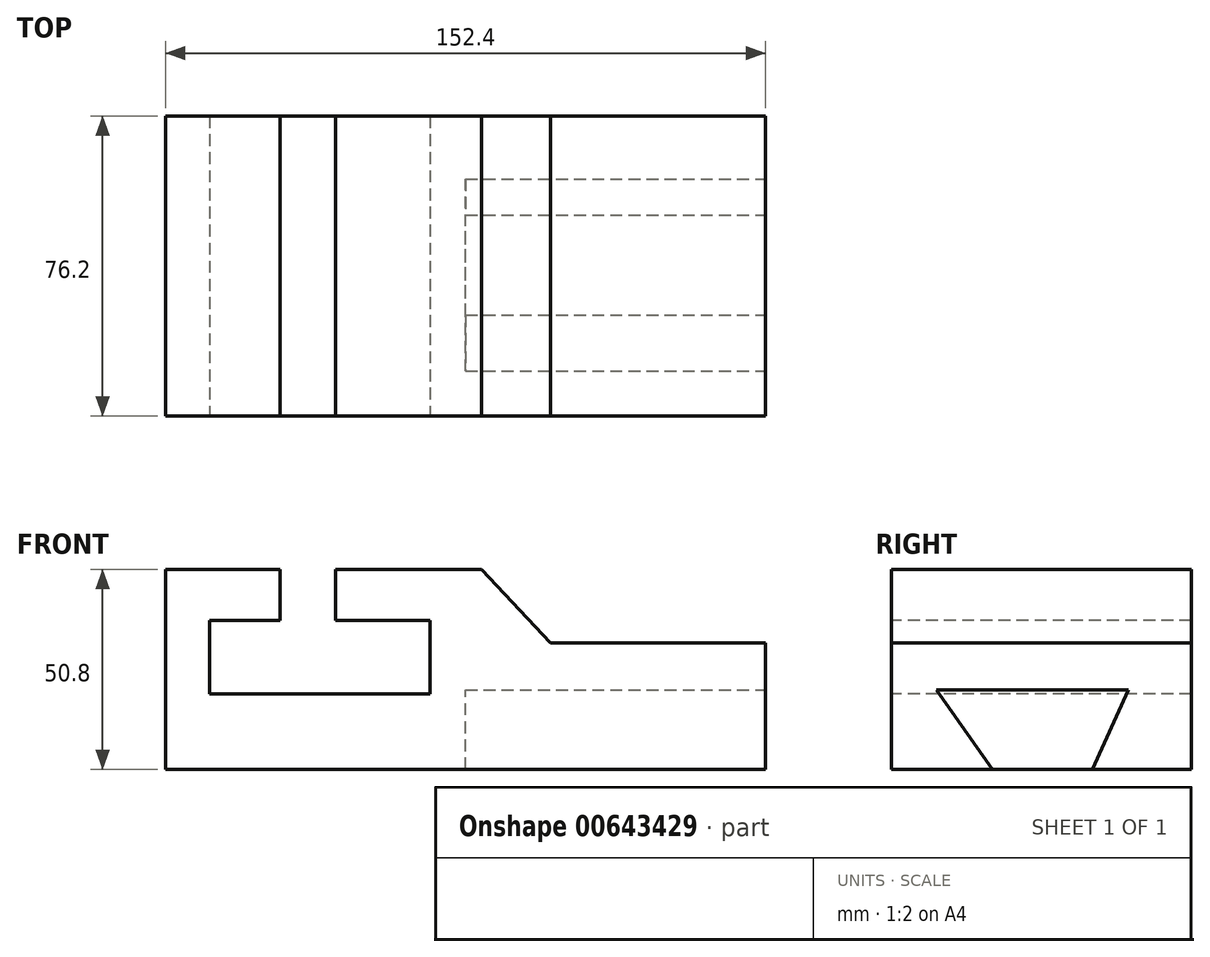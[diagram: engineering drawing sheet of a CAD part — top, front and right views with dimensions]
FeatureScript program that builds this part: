
annotation { "Feature Type Name" : "Feature", "Feature Type Description" : "" }
export const myFeature = defineFeature(function(context is Context, id is Id, definition is map)
    precondition{}
    {
        {
            var Q0;
            Q0=qCreatedBy(makeId("Top.planeOp"),FACE);
            var sketch = newSketch(context, id + "F0", { "sketchPlane" : qUnion([Q0])});
            skLineSegment(sketch, "E0.bottom", {"start": v(138.22, -2.13) * mm, "end": v(290.62, -2.13) * mm});
            skLineSegment(sketch, "E0.top", {"start": v(138.22, 74.07) * mm, "end": v(290.62, 74.07) * mm});
            skLineSegment(sketch, "E0.left", {"start": v(138.22, -2.13) * mm, "end": v(138.22, 74.07) * mm});
            skLineSegment(sketch, "E0.right", {"start": v(290.62, -2.13) * mm, "end": v(290.62, 74.07) * mm});
            skSolve(sketch);
        }
        {
            var Q0;
            Q0=makeQuery(id+"F0.imprint","IMPRINT",FACE,{"disambiguationData":[TD([[makeQuery(id+"F0.imprint","IMPRINT",EDGE,{"derivedFrom":sQuery(id+"F0.wireOp",EDGE,"E0.bottom")}),1.0]])]});
            extrude(context, id + "F1", {"entities" : qUnion([Q0]), "depth" : 50.8 * mm, "offsetDistance" : 25.4 * mm});
        }
        {
            var Q0;
            Q0=makeQuery(id+"F1.opExtrude","SWEPT_FACE",FACE,{"disambiguationData":[OSD([sQuery(id+"F0.wireOp",EDGE,"E0.bottom")])]});
            var sketch = newSketch(context, id + "F2", { "sketchPlane" : qUnion([Q0])});
            skLineSegment(sketch, "E1", {"start": v(138.22, 50.8) * mm, "end": v(167.32, 50.8) * mm});
            skLineSegment(sketch, "E2", {"start": v(167.32, 50.8) * mm, "end": v(167.32, 37.91) * mm});
            skLineSegment(sketch, "E3", {"start": v(167.32, 37.91) * mm, "end": v(149.44, 37.91) * mm});
            skLineSegment(sketch, "E4", {"start": v(149.44, 37.91) * mm, "end": v(149.44, 19.17) * mm});
            skLineSegment(sketch, "E5", {"start": v(149.44, 19.17) * mm, "end": v(205.37, 19.17) * mm});
            skLineSegment(sketch, "E6", {"start": v(205.37, 19.17) * mm, "end": v(205.37, 37.91) * mm});
            skLineSegment(sketch, "E7", {"start": v(205.37, 37.91) * mm, "end": v(181.45, 37.91) * mm});
            skLineSegment(sketch, "E8", {"start": v(181.45, 37.91) * mm, "end": v(181.45, 50.8) * mm});
            skLineSegment(sketch, "E9", {"start": v(181.45, 50.8) * mm, "end": v(167.32, 50.8) * mm});
            skSolve(sketch);
        }
        {
            var Q0;
            Q0=makeQuery(id+"F2.imprint","IMPRINT",FACE,{"disambiguationData":[TD([[makeQuery(id+"F2.imprint","IMPRINT",EDGE,{"derivedFrom":sQuery(id+"F2.wireOp",EDGE,"E2")}),1.0]])]});
            extrude(context, id + "F3", {"entities" : qUnion([Q0]), "operationType" : NewBodyOperationType.REMOVE, "oppositeDirection" : true, "depth" : 76.2 * mm, "offsetDistance" : 25.4 * mm});
        }
        {
            var Q0;
            Q0=makeQuery(id+"F1.opExtrude","SWEPT_FACE",FACE,{"disambiguationData":[OSD([sQuery(id+"F0.wireOp",EDGE,"E0.bottom")])]});
            var sketch = newSketch(context, id + "F4", { "sketchPlane" : qUnion([Q0])});
            skLineSegment(sketch, "E10", {"start": v(218.44, 50.8) * mm, "end": v(236.03, 32.16) * mm});
            skPoint(sketch, "E10.endSnap0", {"position": v(236.03, 50.8) * mm});
            skLineSegment(sketch, "E11", {"start": v(236.03, 32.16) * mm, "end": v(290.62, 32.16) * mm});
            skLineSegment(sketch, "E12", {"start": v(290.62, 32.16) * mm, "end": v(290.62, 50.8) * mm});
            skLineSegment(sketch, "E13", {"start": v(290.62, 50.8) * mm, "end": v(218.44, 50.8) * mm});
            skSolve(sketch);
        }
        {
            var Q0;
            Q0=makeQuery(id+"F4.imprint","IMPRINT",FACE,{"disambiguationData":[TD([[makeQuery(id+"F4.imprint","IMPRINT",EDGE,{"derivedFrom":sQuery(id+"F4.wireOp",EDGE,"E10")}),1.0]])]});
            extrude(context, id + "F5", {"entities" : qUnion([Q0]), "operationType" : NewBodyOperationType.REMOVE, "oppositeDirection" : true, "depth" : 76.2 * mm, "offsetDistance" : 25.4 * mm});
        }
        {
            var Q0;
            Q0=makeQuery(id+"F1.opExtrude","SWEPT_FACE",FACE,{"disambiguationData":[OSD([sQuery(id+"F0.wireOp",EDGE,"E0.right")])]});
            var sketch = newSketch(context, id + "F6", { "sketchPlane" : qUnion([Q0])});
            skLineSegment(sketch, "E14", {"start": v(23.5, 0) * mm, "end": v(9.27, 20.2) * mm});
            skLineSegment(sketch, "E15", {"start": v(9.27, 20.2) * mm, "end": v(58.04, 20.2) * mm});
            skLineSegment(sketch, "E16", {"start": v(58.04, 20.2) * mm, "end": v(48.9, 0) * mm});
            skLineSegment(sketch, "E17", {"start": v(48.9, 0) * mm, "end": v(23.5, 0) * mm});
            skSolve(sketch);
        }
        {
            var Q0;
            Q0=makeQuery(id+"F6.imprint","IMPRINT",FACE,{"disambiguationData":[TD([[makeQuery(id+"F6.imprint","IMPRINT",EDGE,{"derivedFrom":sQuery(id+"F6.wireOp",EDGE,"E14")}),-1.0]])]});
            extrude(context, id + "F7", {"entities" : qUnion([Q0]), "operationType" : NewBodyOperationType.REMOVE, "oppositeDirection" : true, "depth" : 76.2 * mm, "offsetDistance" : 25.4 * mm});
        }
    });
